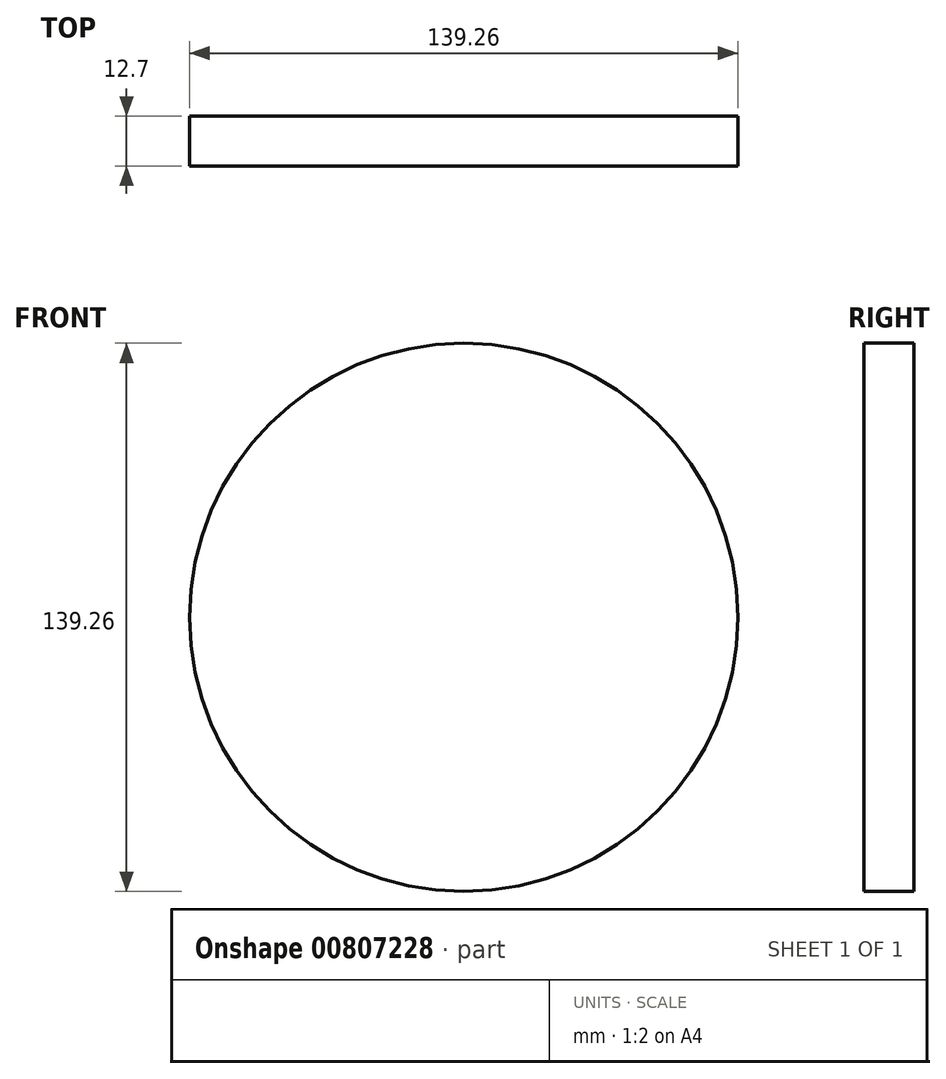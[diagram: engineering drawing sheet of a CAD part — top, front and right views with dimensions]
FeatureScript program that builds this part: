
annotation { "Feature Type Name" : "Feature", "Feature Type Description" : "" }
export const myFeature = defineFeature(function(context is Context, id is Id, definition is map)
    precondition{}
    {
        {
            var Q0;
            Q0=qCreatedBy(makeId("Front.planeOp"),FACE);
            var sketch = newSketch(context, id + "F0", { "sketchPlane" : qUnion([Q0])});
            skCircle(sketch, "E0", {"center": v(0, 0) * mm, "radius": 69.63 * mm});
            skSolve(sketch);
        }
        {
            var Q0;
            Q0 = qSketchRegion(id + "F0", true);
            extrude(context, id + "F1", {"entities" : qUnion([Q0]), "depth" : 12.7 * mm, "offsetDistance" : 25.4 * mm});
        }
    });
